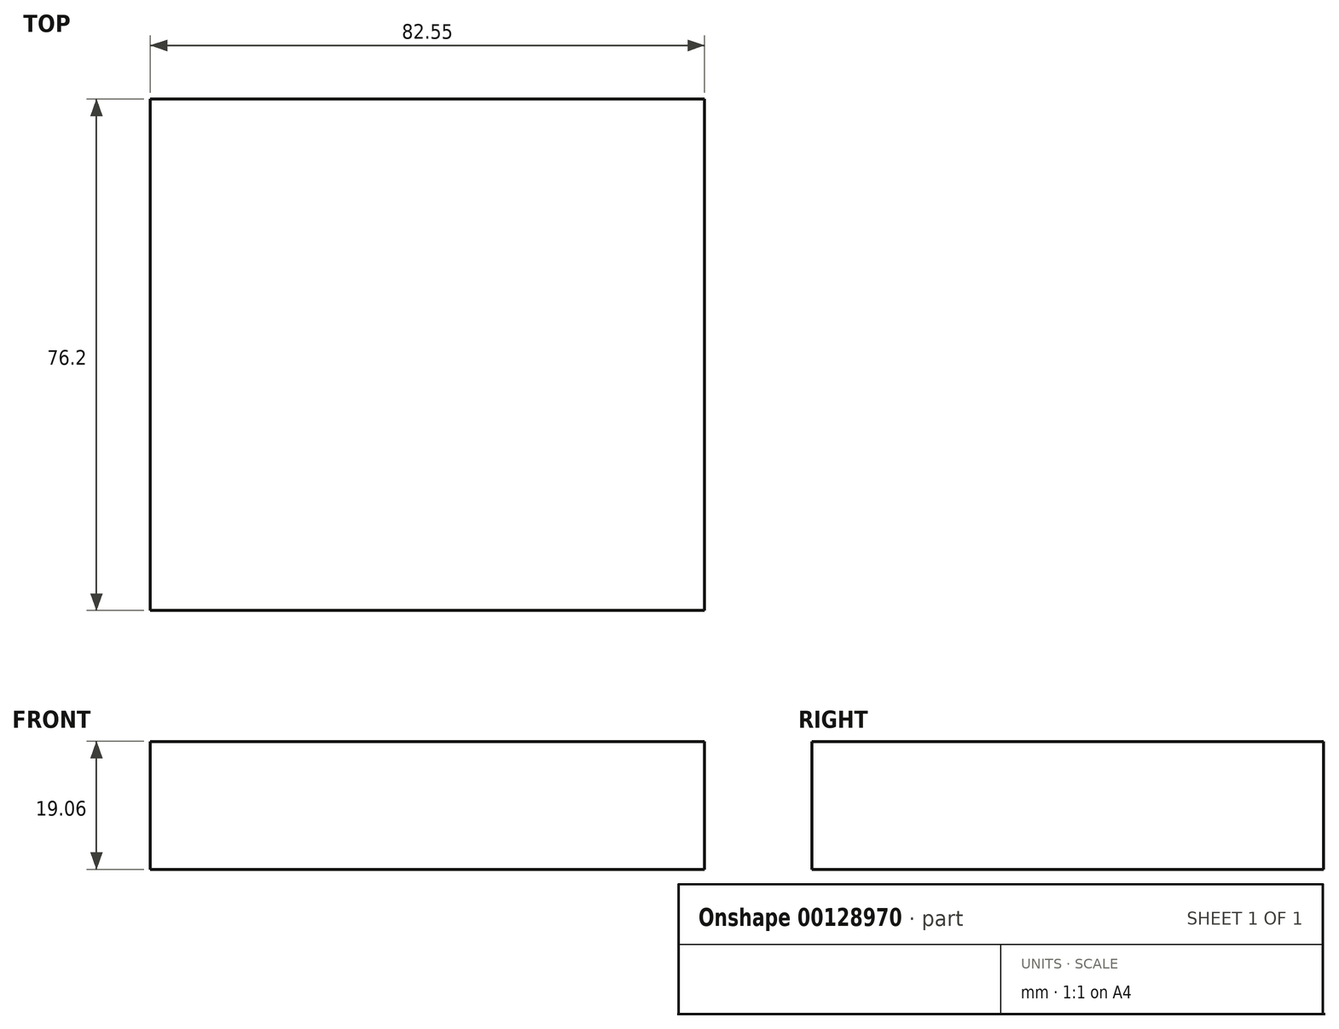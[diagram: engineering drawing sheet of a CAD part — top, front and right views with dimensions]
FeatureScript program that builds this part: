
annotation { "Feature Type Name" : "Feature", "Feature Type Description" : "" }
export const myFeature = defineFeature(function(context is Context, id is Id, definition is map)
    precondition{}
    {
        {
            var Q0;
            Q0=qCreatedBy(makeId("Front.planeOp"),FACE);
            var sketch = newSketch(context, id + "F0", { "sketchPlane" : qUnion([Q0])});
            skLineSegment(sketch, "E0.bottom", {"start": v(41.27, 9.53) * mm, "end": v(-41.28, 9.53) * mm});
            skLineSegment(sketch, "E0.top", {"start": v(41.28, -9.52) * mm, "end": v(-41.27, -9.52) * mm});
            skLineSegment(sketch, "E0.left", {"start": v(41.28, 9.53) * mm, "end": v(41.28, -9.52) * mm});
            skLineSegment(sketch, "E0.right", {"start": v(-41.28, 9.53) * mm, "end": v(-41.27, -9.52) * mm});
            skPoint(sketch, "E0.middle", {"position": v(0, 0) * mm});
            skLineSegment(sketch, "E1.bottom", {"start": v(102.6, 63.16) * mm, "end": v(51.8, 63.16) * mm});
            skLineSegment(sketch, "E1.top", {"start": v(102.6, 91.73) * mm, "end": v(51.8, 91.73) * mm});
            skLineSegment(sketch, "E1.left", {"start": v(102.6, 63.16) * mm, "end": v(102.6, 91.73) * mm});
            skLineSegment(sketch, "E1.right", {"start": v(51.8, 63.16) * mm, "end": v(51.8, 91.73) * mm});
            skPoint(sketch, "E1.middle", {"position": v(77.2, 77.45) * mm});
            skLineSegment(sketch, "E2", {"start": v(41.27, 9.53) * mm, "end": v(41.27, 49.8) * mm});
            skArc(sketch, "E3", {"start": v(41.27, 49.8) * mm, "mid": v(45.92, 61.02) * mm, "end": v(57.15, 65.67) * mm});
            skLineSegment(sketch, "E4", {"start": v(57.15, 65.67) * mm, "end": v(82.32, 65.67) * mm});
            skLineSegment(sketch, "E5.0", {"start": v(57.15, 84.72) * mm, "end": v(82.32, 84.72) * mm});
            skArc(sketch, "E5.1", {"start": v(22.23, 49.8) * mm, "mid": v(32.45, 74.5) * mm, "end": v(57.15, 84.72) * mm});
            skLineSegment(sketch, "E5.2", {"start": v(22.22, 9.53) * mm, "end": v(22.22, 49.8) * mm});
            skFitSpline(sketch, "E6", {"points": [v(-41.28, 9.52) * mm, v(57.15, 84.72) * mm], "startDerivative": vector(63.18, 110.78) * mm, "endDerivative": vector(149.37, 4.5) * mm});
            skSolve(sketch);
        }
        {
            var Q0;
            Q0=makeQuery(id+"F0.imprint","IMPRINT",FACE,{"disambiguationData":[TD([[makeQuery(id+"F0.imprint","IMPRINT",EDGE,{"derivedFrom":sQuery(id+"F0.wireOp",EDGE,"E0.top")}),-1.0]])]});
            extrude(context, id + "F1", {"entities" : qUnion([Q0]), "endBound" : BoundingType.SYMMETRIC, "depth" : 76.2 * mm});
        }
    });
